# Revit family: LED FRAME 05_LZFSBWW
name_source: partatom
category: Luminarias
units: mm (PartAtom-declared; Revit-internal decimal feet)

## family parameters
Compartido = No
Corte con vacíos al cargar = No
Cota de conector redondo = Diámetro de uso
Origen de luz = Sí
Punto de cálculo de habitación = No
Se basa en plano de trabajo = Sí
Siempre vertical = No
Tipo de pieza = Normal

## types (1)
- LED FRAME 05_LZFSBWW
    Cambio de temperatura de color de luz atenuada = <Ninguno>
    Comentarios de vataje = 90-240V
    Descripción = LUMINARIA DIRIGIBLE TIPO ARBOTANTE, ACABADO EN ALUMINIO CON UN PESO DE 0.70KG, CON 4 LED TIPO CREE Y UNA POTENCIA DE 5W, 320 LUMENES, TEMPERATURA EN BLANCO CALIDO 3000K, IRC 80, IP 20, APERTURA DE 45 GRADOS, CORRIENTE DE OPERACIÓN 39mA, CABLE DE 6.7CM, ALIMENTADO A 90-240VAC
    Elevación por defecto = 0 mm  [stored 0 ft]
    Fabricante = BRILLANT
    Filtro de color = 16777215
    Longitud de símbolo de origen de luz = 1500 mm  [stored 4.92126 ft]
    Lámpara = CREE
    Modelo = LZFSBWW
    Watt per fixture = 5
    Ángulo de campo de foco = 45.00°
    Ángulo de enfoque = 45.00°
    Ángulo de inclinación = 60.00°

note: [stored X ft] marks values corroborated as IEEE doubles in the binary element streams (Revit-internal decimal feet)

## geometry (parser evidence)
native form markers: Blend x2
no freeform markers — native parametric forms only
